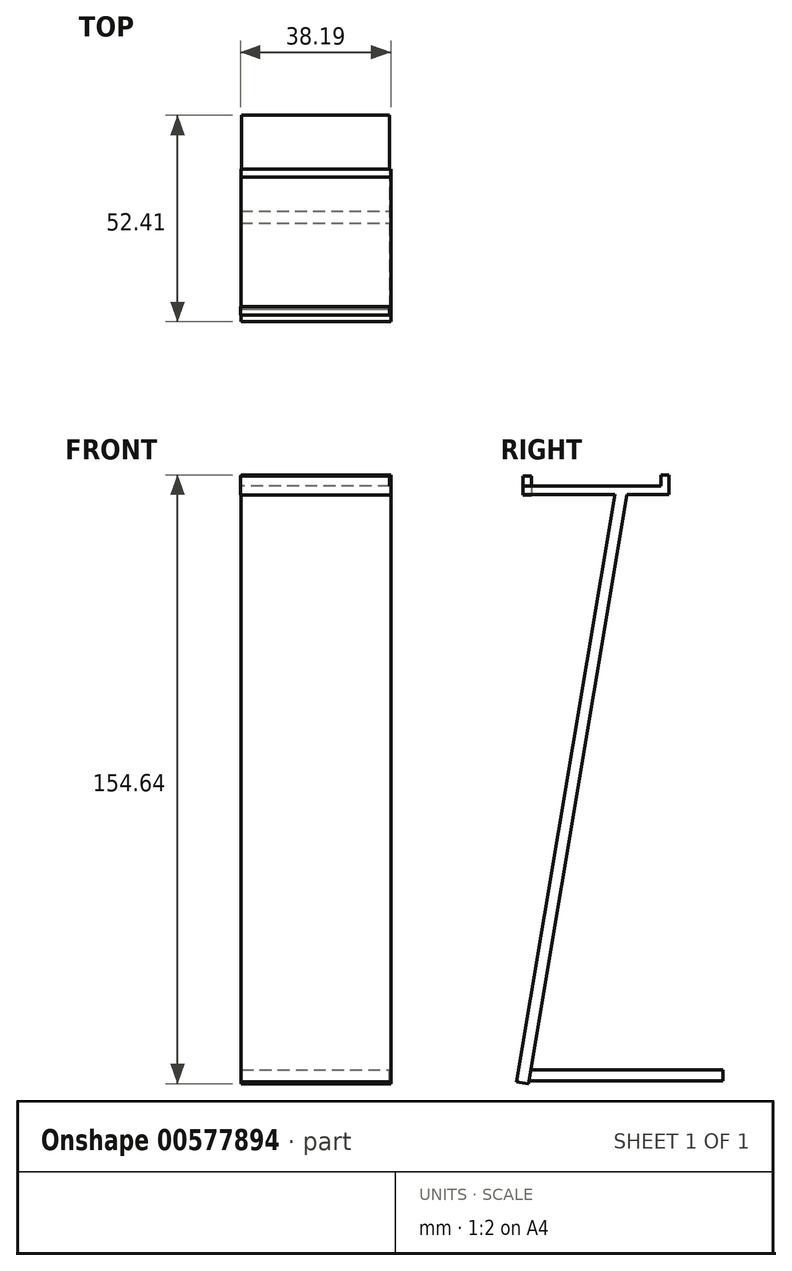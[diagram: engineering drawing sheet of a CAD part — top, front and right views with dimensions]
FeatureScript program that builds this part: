
annotation { "Feature Type Name" : "Feature", "Feature Type Description" : "" }
export const myFeature = defineFeature(function(context is Context, id is Id, definition is map)
    precondition{}
    {
        {
            var Q0;
            Q0=qCreatedBy(makeId("Right.planeOp"),FACE);
            var sketch = newSketch(context, id + "F0", { "sketchPlane" : qUnion([Q0])});
            skLineSegment(sketch, "E0.bottom", {"start": v(-1.61, -75.93) * mm, "end": v(1.42, -75.93) * mm});
            skLineSegment(sketch, "E0.top", {"start": v(-1.61, 75.93) * mm, "end": v(1.42, 75.93) * mm});
            skLineSegment(sketch, "E0.left", {"start": v(-1.61, -75.93) * mm, "end": v(-1.61, 75.93) * mm});
            skLineSegment(sketch, "E0.right", {"start": v(1.42, -75.93) * mm, "end": v(1.42, 75.93) * mm});
            skSolve(sketch);
        }
        {
            var Q0;
            Q0=makeQuery(id+"F0.imprint","IMPRINT",FACE,{"disambiguationData":[TD([[makeQuery(id+"F0.imprint","IMPRINT",EDGE,{"derivedFrom":sQuery(id+"F0.wireOp",EDGE,"E0.bottom")}),1.0]])]});
            extrude(context, id + "F1", {"entities" : qUnion([Q0]), "depth" : 19.05 * mm, "offsetDistance" : 25.4 * mm, "hasSecondDirection" : true, "secondDirectionOppositeDirection" : true, "secondDirectionDepth" : 19.05 * mm});
        }
        {
            var Q0;
            Q0=makeQuery(id+"F1.opExtrude","SWEPT_BODY",BODY,{"disambiguationData":[OSD([sQuery(id+"F0.wireOp",EDGE,"E0.bottom"),sQuery(id+"F0.wireOp",EDGE,"E0.top"),sQuery(id+"F0.wireOp",EDGE,"E0.left"),sQuery(id+"F0.wireOp",EDGE,"E0.right")])]});
            var Q1;
            Q1=makeQuery(id+"F1.opExtrude","SWEPT_EDGE",EDGE,{"disambiguationData":[OSD([sQuery(id+"F0.wireOp",EDGE,"E0.bottom"),sQuery(id+"F0.wireOp",EDGE,"E0.left")])]});
            transform(context, id + "F2", {"entities" : qUnion([Q0]), "transformType" : TransformType.ROTATION, "transformAxis" : qUnion([Q1]), "angle" : 9.5 * degree, "makeCopy" : false});
        }
        {
            var Q0;
            Q0=qCreatedBy(makeId("Front.planeOp"),FACE);
            var sketch = newSketch(context, id + "F3", { "sketchPlane" : qUnion([Q0])});
            skLineSegment(sketch, "E1.bottom", {"start": v(-18.86, -75.74) * mm, "end": v(18.68, -75.74) * mm});
            skLineSegment(sketch, "E1.top", {"start": v(-18.86, -72.9) * mm, "end": v(18.68, -72.9) * mm});
            skLineSegment(sketch, "E1.left", {"start": v(-18.86, -75.74) * mm, "end": v(-18.86, -72.9) * mm});
            skLineSegment(sketch, "E1.right", {"start": v(18.68, -75.74) * mm, "end": v(18.68, -72.9) * mm});
            skSolve(sketch);
        }
        {
            var Q0;
            Q0 = qSketchRegion(id + "F3", true);
            extrude(context, id + "F4", {"entities" : qUnion([Q0]), "operationType" : NewBodyOperationType.ADD, "depth" : -50.8 * mm, "offsetDistance" : 25.4 * mm});
        }
        {
            var Q0;
            Q0=qCreatedBy(makeId("Right.planeOp"),FACE);
            var sketch = newSketch(context, id + "F5", { "sketchPlane" : qUnion([Q0])});
            skLineSegment(sketch, "E2.bottom", {"start": v(36.93, 73.27) * mm, "end": v(0, 73.27) * mm});
            skLineSegment(sketch, "E2.top", {"start": v(36.93, 75.36) * mm, "end": v(0, 75.36) * mm});
            skLineSegment(sketch, "E2.left", {"start": v(36.93, 73.27) * mm, "end": v(36.93, 75.36) * mm});
            skLineSegment(sketch, "E2.right", {"start": v(0, 73.27) * mm, "end": v(0, 75.36) * mm});
            skSolve(sketch);
        }
        {
            var Q0;
            Q0=makeQuery(id+"F5.imprint","IMPRINT",FACE,{"disambiguationData":[TD([[makeQuery(id+"F5.imprint","IMPRINT",EDGE,{"derivedFrom":sQuery(id+"F5.wireOp",EDGE,"E2.bottom")}),-1.0]])]});
            extrude(context, id + "F6", {"entities" : qUnion([Q0]), "operationType" : NewBodyOperationType.ADD, "depth" : 19.05 * mm, "offsetDistance" : 25.4 * mm, "hasSecondDirection" : true, "secondDirectionOppositeDirection" : true, "secondDirectionDepth" : 19.05 * mm});
        }
        {
            var Q0;
            Q0=qCreatedBy(makeId("Right.planeOp"),FACE);
            var sketch = newSketch(context, id + "F7", { "sketchPlane" : qUnion([Q0])});
            skLineSegment(sketch, "E3.bottom", {"start": v(37.12, 73.27) * mm, "end": v(35.03, 73.27) * mm});
            skLineSegment(sketch, "E3.top", {"start": v(37.12, 78.21) * mm, "end": v(35.03, 78.21) * mm});
            skLineSegment(sketch, "E3.left", {"start": v(37.12, 73.27) * mm, "end": v(37.12, 78.21) * mm});
            skLineSegment(sketch, "E3.right", {"start": v(35.03, 73.27) * mm, "end": v(35.03, 78.21) * mm});
            skSolve(sketch);
        }
        {
            var Q0;
            Q0=makeQuery(id+"F7.imprint","IMPRINT",FACE,{"disambiguationData":[TD([[makeQuery(id+"F7.imprint","IMPRINT",EDGE,{"derivedFrom":sQuery(id+"F7.wireOp",EDGE,"E3.bottom")}),-1.0]])]});
            extrude(context, id + "F8", {"entities" : qUnion([Q0]), "operationType" : NewBodyOperationType.ADD, "depth" : 19.05 * mm, "offsetDistance" : 25.4 * mm, "hasSecondDirection" : true, "secondDirectionOppositeDirection" : true, "secondDirectionDepth" : 19.05 * mm});
        }
        {
            var Q0;
            Q0=qCreatedBy(makeId("Front.planeOp"),FACE);
            var sketch = newSketch(context, id + "F9", { "sketchPlane" : qUnion([Q0])});
            skLineSegment(sketch, "E4.bottom", {"start": v(-19.14, 73.13) * mm, "end": v(18.76, 73.13) * mm});
            skLineSegment(sketch, "E4.top", {"start": v(-19.14, 77.94) * mm, "end": v(18.76, 77.94) * mm});
            skLineSegment(sketch, "E4.left", {"start": v(-19.14, 73.13) * mm, "end": v(-19.14, 77.94) * mm});
            skLineSegment(sketch, "E4.right", {"start": v(18.76, 73.13) * mm, "end": v(18.76, 77.94) * mm});
            skSolve(sketch);
        }
        {
            var Q0;
            Q0=makeQuery(id+"F9.imprint","IMPRINT",FACE,{"disambiguationData":[TD([[makeQuery(id+"F9.imprint","IMPRINT",EDGE,{"derivedFrom":sQuery(id+"F9.wireOp",EDGE,"E4.bottom")}),1.0]])]});
            extrude(context, id + "F10", {"entities" : qUnion([Q0]), "operationType" : NewBodyOperationType.ADD, "oppositeDirection" : true, "depth" : 2.13 * mm, "offsetDistance" : 25.4 * mm});
        }
    });
